MODEL slx_677b603a2b6e
CONFIG AbsTol = auto
CONFIG EnableMultiTasking = off
CONFIG FixedStep = auto
CONFIG InitFcn = Wn = 10;

T = 0.001;

Kp = 1.5;
Ki = 0.2;
Kd = 0.001;
CONFIG MaxStep = auto
CONFIG MinStep = auto
CONFIG RelTol = 1e-3
CONFIG SampleTimeConstraint = Unconstrained
CONFIG SolverName = VariableStepAuto
CONFIG StartTime = 0.0
CONFIG StopTime = 10.0
BLOCK [CCaller] C Caller2
  FunctionName = PID_Loop
  PortSpecificationStruct = %)30     .    X ,   8    (     @         %    "     (    !     0         %  0 "0    $    _    07)G3F%M90  4&]R=$YA;64 4V-O<&4     26YD97@     5'EP90      4VEZ90      27-';&]B86P   X    X    !@    @    $          4    (     0    4    !         !     %    97)R;W(    .    .     8    (    !          %    "     $    %     0         0    !0   &5R<F]R    #@   #@    &    "     0         !0    @    !    !0...<+936ch>
BLOCK [DataTypeConversion] Data Type Conversion2
  RndMeth = Floor
  SaturateOnIntegerOverflow = off
BLOCK [Derivative] Derivative1
BLOCK [DiscreteTransferFcn] Discrete Transfer Fcn13
  CloseFcn = dspblkCoreblockFVToolHelper(gcbh,'close');
  CopyFcn = dspblkCoreblockFVToolHelper(gcbh,'copy');
  DeleteFcn = dspblkCoreblockFVToolHelper(gcbh,'close');
  Denominator = [2+T*Wn -2+T*Wn]
  InputPortMap = u0
  LoadFcn = dspblkCoreblockFVToolHelper(gcbh,'load');
  ModelCloseFcn = dspblkCoreblockFVToolHelper(gcbh,'close');
  Numerator = [2*Wn -2*Wn]
  PostSaveFcn = dspblkCoreblockFVToolHelper(gcbh,'postsave');
  PreSaveFcn = dspblkCoreblockFVToolHelper(gcbh,'presave');
BLOCK [DiscreteTransferFcn] Discrete Transfer Fcn14
  CloseFcn = dspblkCoreblockFVToolHelper(gcbh,'close');
  CopyFcn = dspblkCoreblockFVToolHelper(gcbh,'copy');
  DeleteFcn = dspblkCoreblockFVToolHelper(gcbh,'close');
  Denominator = [2 -2]
  InputPortMap = u0
  LoadFcn = dspblkCoreblockFVToolHelper(gcbh,'load');
  ModelCloseFcn = dspblkCoreblockFVToolHelper(gcbh,'close');
  Numerator = [T T]
  PostSaveFcn = dspblkCoreblockFVToolHelper(gcbh,'postsave');
  PreSaveFcn = dspblkCoreblockFVToolHelper(gcbh,'presave');
BLOCK [DiscreteTransferFcn] Discrete Transfer Fcn15
  CloseFcn = dspblkCoreblockFVToolHelper(gcbh,'close');
  CopyFcn = dspblkCoreblockFVToolHelper(gcbh,'copy');
  DeleteFcn = dspblkCoreblockFVToolHelper(gcbh,'close');
  Denominator = [(4+2*T*Wn) -8 4-2*T*Wn]
  InputPortMap = u0
  LoadFcn = dspblkCoreblockFVToolHelper(gcbh,'load');
  ModelCloseFcn = dspblkCoreblockFVToolHelper(gcbh,'close');
  Numerator = [(4*Kp+2*Ki*T+4*Kd*Wn+2*Kp*T*Wn+Ki*Wn*T^2) (-8*Kp-8*Kd*Wn+2*Ki*Wn*T^2) (4*Kp-2*Ki*T+4*Kd*Wn-2*Kp*T*Wn+Ki*Wn*T^2)]
  PostSaveFcn = dspblkCoreblockFVToolHelper(gcbh,'postsave');
  PreSaveFcn = dspblkCoreblockFVToolHelper(gcbh,'presave');
BLOCK [Gain] Gain15
  Gain = Kd
BLOCK [Gain] Gain21
  Gain = Kd
BLOCK [Gain] Gain22
  Gain = Ki
BLOCK [Gain] Gain23
  Gain = Kp
BLOCK [Gain] Gain24
  Gain = Ki
BLOCK [Gain] Gain25
  Gain = Kp
BLOCK [Scope] Scope11
  ActiveDisplayYMaximum = 3.5506703969871358
  ActiveDisplayYMinimum = 0.057080287750086
  DataLoggingVariableName = ScopeData12
  Floating = off
  GraphicalSettings = {"Style":{"BackgroundColor":[0.12941176470588237,0.12941176470588237,0.12941176470588237],"AxesColor":[0.07058823529411765,0.07058823529411765,0.07058823529411765],"LabelsColor":[0.8509803921568627,0.8509803921568627,0.8509803921568627],"PreserveColors":false,"Visible":[true,true,true,true],"LineStyle":["-","-","-","-"],"LineWidth":[1.5,1.5,1.5,1.5],"BarWidth":[0.9,0.9,0.9,0.9],"LineColor":["auto"...<+2394ch>
  MultipleDisplayCache = [{"MaxYLimMag":6.0001124999983722,"MaxYLimReal":3.5506703969871358,"MinYLimMag":0.999987500000181,"MinYLimReal":0.057080287750086,"PlotAsMagnitudePhase":false,"ShowGrid":true,"ShowLegend":true,"Title":"%<SignalLabel>","YLabel":""}]
  NumInputPorts = 4
  ScopeFrameLocation = window
  ShowLegend = on
  WasSavedAsWebScope = on
  WindowPosition = [912.000000,308.000000,720.000000,517.000000,]
BLOCK [Sin] Sine Wave23
  Amplitude = 0.5
  Bias = 0.5
  SampleTime = 0
BLOCK [Sum] Sum11
  Inputs = +++
BLOCK [Sum] Sum12
  Inputs = +++
BLOCK [TransferFcn] Transfer Fcn19
  Denominator = [1 0]
BLOCK [ZeroOrderHold] Zero-Order Hold8
  SampleTime = 0.001
LINE C Caller2:1 -> Scope11:4
LINE Data Type Conversion2:1 -> C Caller2:1
LINE Derivative1:1 -> Sum12:3
LINE Discrete Transfer Fcn13:1 -> Sum11:3
LINE Discrete Transfer Fcn14:1 -> Sum11:2
LINE Discrete Transfer Fcn15:1 -> Scope11:3
LINE Gain15:1 -> Derivative1:1
LINE Gain21:1 -> Discrete Transfer Fcn13:1
LINE Gain22:1 -> Discrete Transfer Fcn14:1
LINE Gain23:1 -> Sum11:1
LINE Gain24:1 -> Transfer Fcn19:1
LINE Gain25:1 -> Sum12:1
LINE Sine Wave23:1 -> Gain15:1
LINE Sine Wave23:1 -> Gain24:1
LINE Sine Wave23:1 -> Gain25:1
LINE Sine Wave23:1 -> Zero-Order Hold8:1
LINE Sum11:1 -> Scope11:2
LINE Sum12:1 -> Scope11:1
LINE Transfer Fcn19:1 -> Sum12:2
LINE Zero-Order Hold8:1 -> Data Type Conversion2:1
LINE Zero-Order Hold8:1 -> Discrete Transfer Fcn15:1
LINE Zero-Order Hold8:1 -> Gain21:1
LINE Zero-Order Hold8:1 -> Gain22:1
LINE Zero-Order Hold8:1 -> Gain23:1
